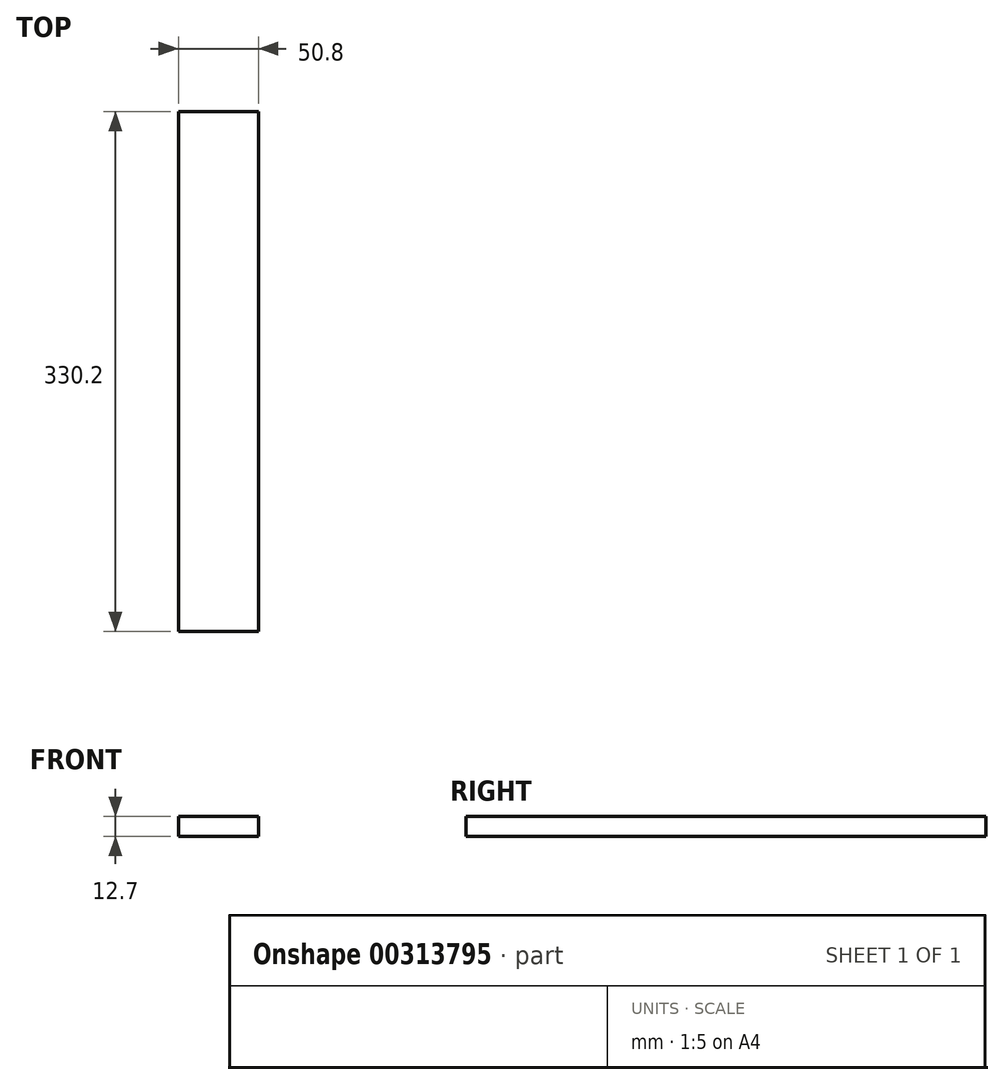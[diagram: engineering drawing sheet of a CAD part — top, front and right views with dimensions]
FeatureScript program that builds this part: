
annotation { "Feature Type Name" : "Feature", "Feature Type Description" : "" }
export const myFeature = defineFeature(function(context is Context, id is Id, definition is map)
    precondition{}
    {
        {
            var Q0;
            Q0=qCreatedBy(makeId("Top.planeOp"),FACE);
            var sketch = newSketch(context, id + "F0", { "sketchPlane" : qUnion([Q0])});
            skLineSegment(sketch, "E0.bottom", {"start": v(0, 0) * mm, "end": v(50.8, 0) * mm});
            skLineSegment(sketch, "E0.top", {"start": v(0, 330.2) * mm, "end": v(50.8, 330.2) * mm});
            skLineSegment(sketch, "E0.left", {"start": v(0, 0) * mm, "end": v(0, 330.2) * mm});
            skLineSegment(sketch, "E0.right", {"start": v(50.8, 0) * mm, "end": v(50.8, 330.2) * mm});
            skSolve(sketch);
        }
        {
            var Q0;
            Q0 = qSketchRegion(id + "F0", true);
            extrude(context, id + "F1", {"entities" : qUnion([Q0]), "depth" : 12.7 * mm});
        }
    });
